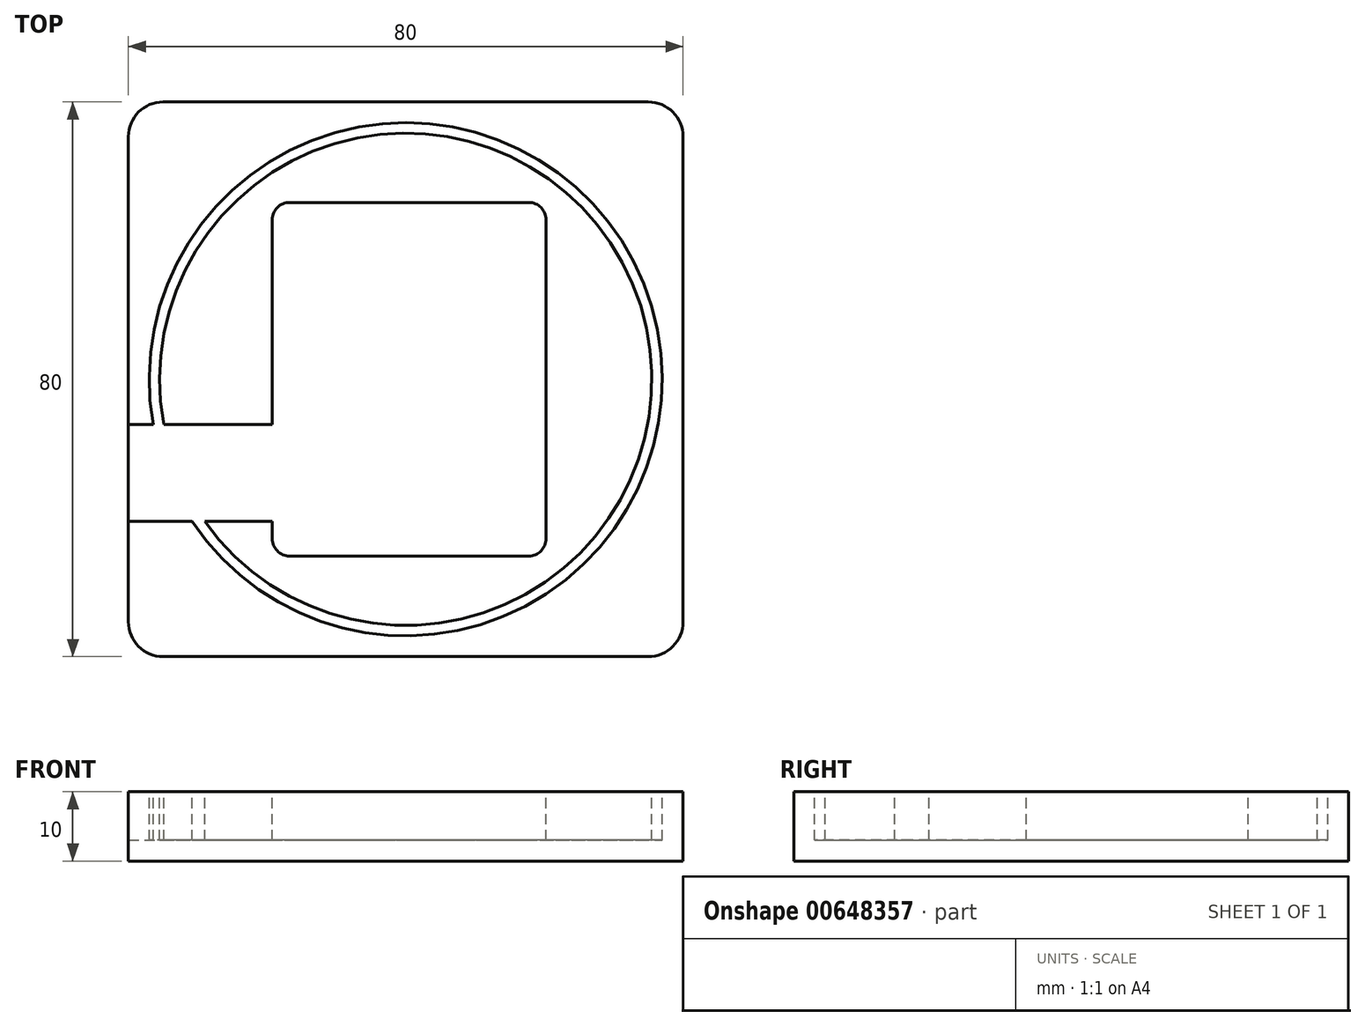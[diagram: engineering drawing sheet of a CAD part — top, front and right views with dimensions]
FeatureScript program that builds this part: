
annotation { "Feature Type Name" : "Feature", "Feature Type Description" : "" }
export const myFeature = defineFeature(function(context is Context, id is Id, definition is map)
    precondition{}
    {
        {
            var Q0;
            Q0=qCreatedBy(makeId("Top.planeOp"),FACE);
            var sketch = newSketch(context, id + "F0", { "sketchPlane" : qUnion([Q0])});
            skLineSegment(sketch, "E0.bottom", {"start": v(5, 80) * mm, "end": v(75, 80) * mm});
            skLineSegment(sketch, "E0.top", {"start": v(5, 0) * mm, "end": v(75, 0) * mm});
            skLineSegment(sketch, "E0.left", {"start": v(0, 75) * mm, "end": v(0, 5) * mm});
            skLineSegment(sketch, "E0.right", {"start": v(80, 75) * mm, "end": v(80, 5) * mm});
            skPoint(sketch, "E1.visualSharp", {"position": v(0, 0) * mm});
            skArc(sketch, "E1.filletArc", {"start": v(0, 5) * mm, "mid": v(1.46, 1.46) * mm, "end": v(5, 0) * mm});
            skPoint(sketch, "E2.visualSharp", {"position": v(80, 0) * mm});
            skArc(sketch, "E2.filletArc", {"start": v(75, 0) * mm, "mid": v(78.54, 1.46) * mm, "end": v(80, 5) * mm});
            skPoint(sketch, "E3.visualSharp", {"position": v(80, 80) * mm});
            skArc(sketch, "E3.filletArc", {"start": v(80, 75) * mm, "mid": v(78.54, 78.54) * mm, "end": v(75, 80) * mm});
            skPoint(sketch, "E4.visualSharp", {"position": v(0, 80) * mm});
            skArc(sketch, "E4.filletArc", {"start": v(5, 80) * mm, "mid": v(1.46, 78.54) * mm, "end": v(0, 75) * mm});
            skSolve(sketch);
        }
        {
            var Q0;
            Q0 = qSketchRegion(id + "F0", true);
            extrude(context, id + "F1", {"entities" : qUnion([Q0]), "depth" : 10 * mm, "offsetDistance" : 25 * mm});
        }
        {
            var Q0;
            Q0=makeQuery(id+"F1.opExtrude","CAP_FACE",FACE,{"disambiguationData":[OSD([sQuery(id+"F0.wireOp",EDGE,"E0.bottom"),sQuery(id+"F0.wireOp",EDGE,"E0.top"),sQuery(id+"F0.wireOp",EDGE,"E0.left"),sQuery(id+"F0.wireOp",EDGE,"E0.right"),sQuery(id+"F0.wireOp",EDGE,"E1.filletArc"),sQuery(id+"F0.wireOp",EDGE,"E2.filletArc"),sQuery(id+"F0.wireOp",EDGE,"E3.filletArc"),sQuery(id+"F0.wireOp",EDGE,"E4.filletArc")])],"isStart":false});
            var sketch = newSketch(context, id + "F2", { "sketchPlane" : qUnion([Q0])});
            skLineSegment(sketch, "E5.bottom", {"start": v(23.25, 14.5) * mm, "end": v(57.75, 14.5) * mm});
            skLineSegment(sketch, "E5.top", {"start": v(23.25, 65.5) * mm, "end": v(57.75, 65.5) * mm});
            skLineSegment(sketch, "E5.left", {"start": v(20.75, 17) * mm, "end": v(20.75, 63) * mm});
            skLineSegment(sketch, "E5.right", {"start": v(60.25, 17) * mm, "end": v(60.25, 63) * mm});
            skPoint(sketch, "E6.visualSharp", {"position": v(20.75, 65.5) * mm});
            skArc(sketch, "E6.filletArc", {"start": v(23.25, 65.5) * mm, "mid": v(21.48, 64.77) * mm, "end": v(20.75, 63) * mm});
            skPoint(sketch, "E7.visualSharp", {"position": v(60.25, 65.5) * mm});
            skArc(sketch, "E7.filletArc", {"start": v(60.25, 63) * mm, "mid": v(59.52, 64.77) * mm, "end": v(57.75, 65.5) * mm});
            skPoint(sketch, "E8.visualSharp", {"position": v(60.25, 14.5) * mm});
            skArc(sketch, "E8.filletArc", {"start": v(57.75, 14.5) * mm, "mid": v(59.52, 15.23) * mm, "end": v(60.25, 17) * mm});
            skPoint(sketch, "E9.visualSharp", {"position": v(20.75, 14.5) * mm});
            skArc(sketch, "E9.filletArc", {"start": v(20.75, 17) * mm, "mid": v(21.48, 15.23) * mm, "end": v(23.25, 14.5) * mm});
            skSolve(sketch);
        }
        {
            var Q0;
            Q0 = qSketchRegion(id + "F2", true);
            extrude(context, id + "F3", {"entities" : qUnion([Q0]), "operationType" : NewBodyOperationType.REMOVE, "oppositeDirection" : true, "depth" : 7 * mm, "offsetDistance" : 25 * mm});
        }
        {
            var Q0;
            Q0=makeQuery(id+"F1.opExtrude","CAP_FACE",FACE,{"disambiguationData":[OSD([sQuery(id+"F0.wireOp",EDGE,"E0.bottom"),sQuery(id+"F0.wireOp",EDGE,"E0.top"),sQuery(id+"F0.wireOp",EDGE,"E0.left"),sQuery(id+"F0.wireOp",EDGE,"E0.right"),sQuery(id+"F0.wireOp",EDGE,"E1.filletArc"),sQuery(id+"F0.wireOp",EDGE,"E2.filletArc"),sQuery(id+"F0.wireOp",EDGE,"E3.filletArc"),sQuery(id+"F0.wireOp",EDGE,"E4.filletArc")])],"isStart":false});
            var sketch = newSketch(context, id + "F4", { "sketchPlane" : qUnion([Q0])});
            skCircle(sketch, "E10", {"center": v(40, 40) * mm, "radius": 37 * mm});
            skCircle(sketch, "E11", {"center": v(40, 40) * mm, "radius": 35.5 * mm});
            skPoint(sketch, "E11.centerSnap0", {"position": v(60.25, 40) * mm});
            skSolve(sketch);
        }
        {
            var Q0;
            Q0=makeQuery(id+"F4.imprint","IMPRINT",FACE,{"disambiguationData":[TD([[makeQuery(id+"F4.imprint","IMPRINT",EDGE,{"derivedFrom":sQuery(id+"F4.wireOp",EDGE,"E10")}),1.0]])]});
            extrude(context, id + "F5", {"entities" : qUnion([Q0]), "operationType" : NewBodyOperationType.REMOVE, "oppositeDirection" : true, "depth" : 7 * mm, "offsetDistance" : 25 * mm});
        }
        {
            var Q0;
            {var subQ0=sQuery(id+"F0.wireOp",EDGE,"E0.left");var subQ1=sQuery(id+"F0.wireOp",EDGE,"E0.top");var subQ2=sQuery(id+"F0.wireOp",EDGE,"E0.right");var subQ3=sQuery(id+"F0.wireOp",EDGE,"E0.bottom");var subQ4=sQuery(id+"F0.wireOp",EDGE,"E1.filletArc");var subQ5=sQuery(id+"F0.wireOp",EDGE,"E2.filletArc");var subQ6=sQuery(id+"F0.wireOp",EDGE,"E3.filletArc");var subQ7=sQuery(id+"F0.wireOp",EDGE,"E4.filletArc");Q0=makeQuery(id+"F5.boolean.opBoolean","SPLIT",FACE,{"disambiguationData":[TD([makeQuery(id+"F1.opExtrude","SWEPT_FACE",FACE,{"disambiguationData":[OSD([subQ3])]})])],"derivedFrom":makeQuery(id+"F1.opExtrude","CAP_FACE",FACE,{"disambiguationData":[OSD([subQ3,subQ1,subQ0,subQ2,subQ4,subQ5,subQ6,subQ7])],"isStart":false})});}
            var sketch = newSketch(context, id + "F6", { "sketchPlane" : qUnion([Q0])});
            skLineSegment(sketch, "E12.bottom", {"start": v(0, 19.5) * mm, "end": v(20.75, 19.5) * mm});
            skLineSegment(sketch, "E12.top", {"start": v(0, 33.5) * mm, "end": v(20.75, 33.5) * mm});
            skLineSegment(sketch, "E12.left", {"start": v(0, 19.5) * mm, "end": v(0, 33.5) * mm});
            skLineSegment(sketch, "E12.right", {"start": v(20.75, 19.5) * mm, "end": v(20.75, 33.5) * mm});
            skSolve(sketch);
        }
        {
            var Q0;
            Q0 = qSketchRegion(id + "F6", true);
            extrude(context, id + "F7", {"entities" : qUnion([Q0]), "operationType" : NewBodyOperationType.REMOVE, "oppositeDirection" : true, "depth" : 7 * mm, "offsetDistance" : 25 * mm});
        }
    });
